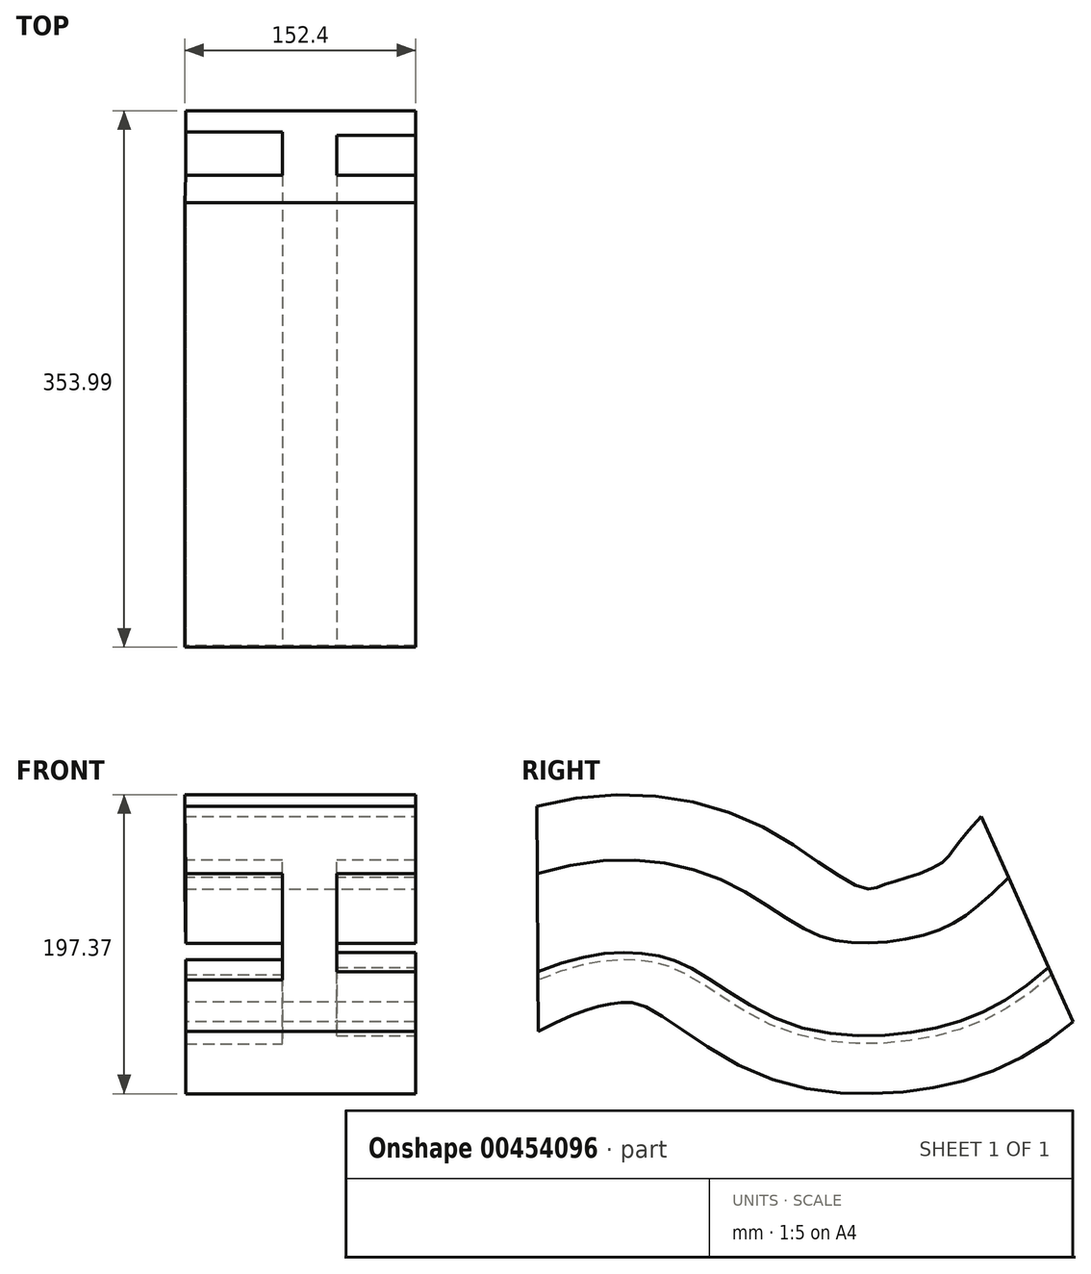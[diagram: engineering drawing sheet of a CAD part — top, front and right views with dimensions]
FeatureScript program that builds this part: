
annotation { "Feature Type Name" : "Feature", "Feature Type Description" : "" }
export const myFeature = defineFeature(function(context is Context, id is Id, definition is map)
    precondition{}
    {
        {
            var Q0;
            Q0=qCreatedBy(makeId("Front.planeOp"),FACE);
            var sketch = newSketch(context, id + "F0", { "sketchPlane" : qUnion([Q0])});
            skLineSegment(sketch, "E0", {"start": v(-75.07, 75.07) * mm, "end": v(77.33, 75.07) * mm});
            skLineSegment(sketch, "E1", {"start": v(77.33, 75.07) * mm, "end": v(77.33, 30.62) * mm});
            skLineSegment(sketch, "E2", {"start": v(77.33, 30.62) * mm, "end": v(25.21, 30.62) * mm});
            skLineSegment(sketch, "E3", {"start": v(25.21, 30.62) * mm, "end": v(25.21, -34.28) * mm});
            skLineSegment(sketch, "E4", {"start": v(25.21, -34.28) * mm, "end": v(77.33, -34.28) * mm});
            skLineSegment(sketch, "E5", {"start": v(77.33, -34.28) * mm, "end": v(77.33, -73.65) * mm});
            skLineSegment(sketch, "E6", {"start": v(77.33, -73.65) * mm, "end": v(-74.5, -73.65) * mm});
            skLineSegment(sketch, "E7", {"start": v(-74.5, -73.65) * mm, "end": v(-74.5, -39.66) * mm});
            skLineSegment(sketch, "E8", {"start": v(-74.5, -39.66) * mm, "end": v(-10.76, -39.66) * mm});
            skLineSegment(sketch, "E9", {"start": v(-10.76, -39.66) * mm, "end": v(-10.76, 30.62) * mm});
            skLineSegment(sketch, "E10", {"start": v(-10.76, 30.62) * mm, "end": v(-74.5, 30.62) * mm});
            skLineSegment(sketch, "E11", {"start": v(-74.5, 30.62) * mm, "end": v(-75.07, 75.07) * mm});
            skSolve(sketch);
        }
        {
            var Q0;
            Q0=qCreatedBy(makeId("Right.planeOp"),FACE);
            var sketch = newSketch(context, id + "F1", { "sketchPlane" : qUnion([Q0])});
            skFitSpline(sketch, "E12", {"points": [v(-1.28, 0) * mm, v(107.61, 0) * mm, v(177.66, -38.06) * mm, v(258.2, -38.26) * mm, v(322.03, 0) * mm], "startDerivative": vector(451.83, 158.7) * mm, "endDerivative": vector(297.3, 277.78) * mm});
            skSolve(sketch);
        }
        {
            var Q0;
            Q0 = qSketchRegion(id + "F0", true);
            var Q1;
            Q1=sQuery(id+"F1.wireOp",EDGE,"E12");
            sweep(context, id + "F2", {"profiles" : qUnion([Q0]), "path" : qUnion([Q1])});
        }
    });
